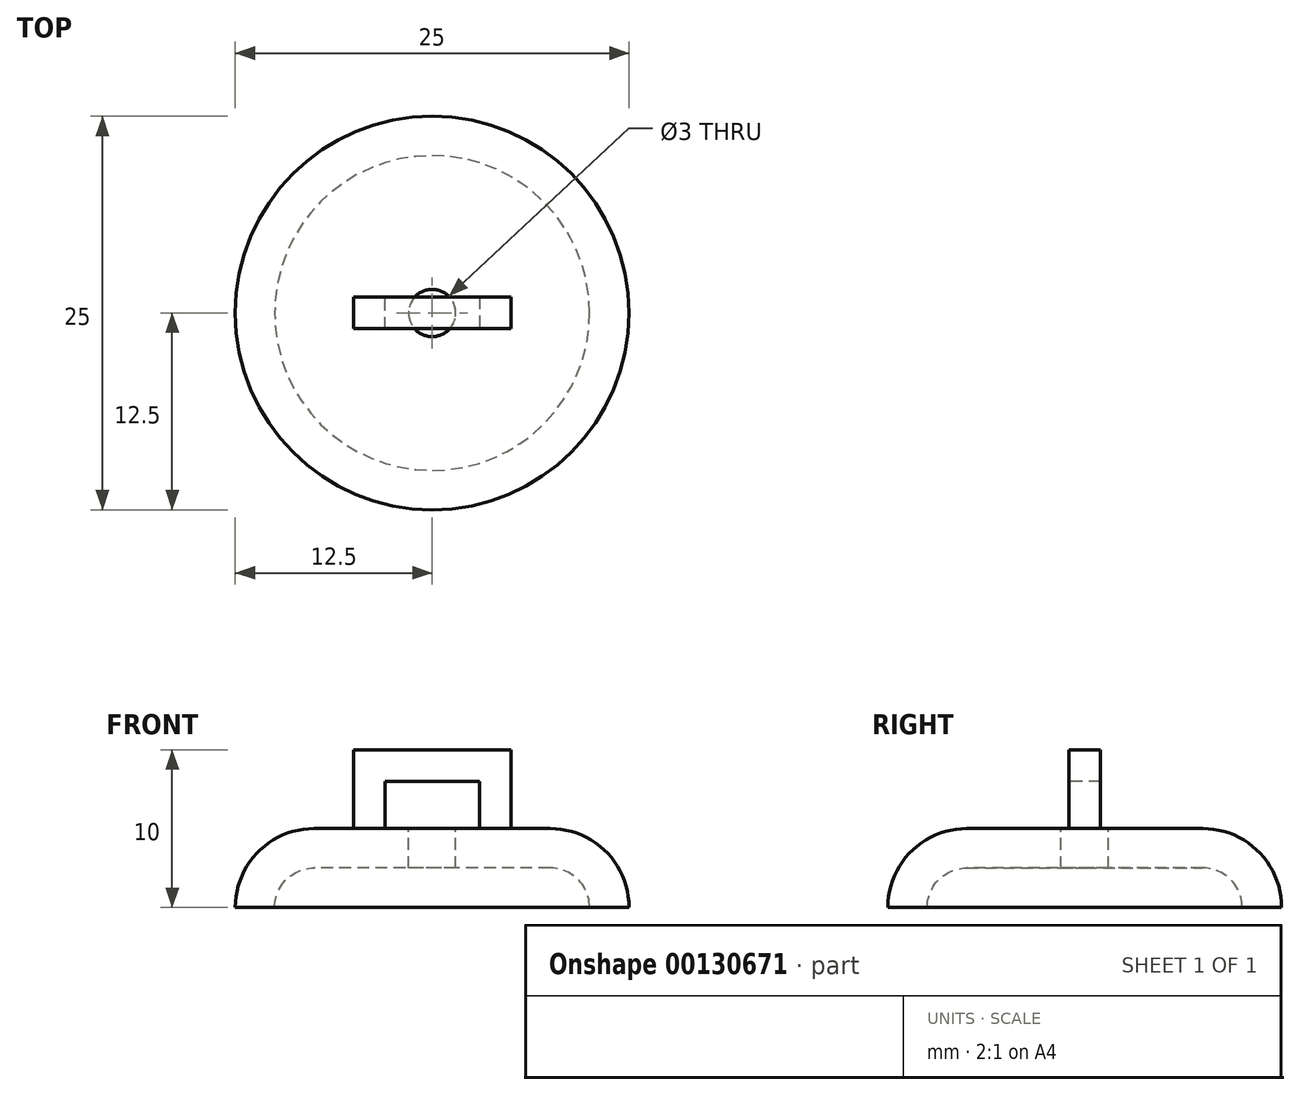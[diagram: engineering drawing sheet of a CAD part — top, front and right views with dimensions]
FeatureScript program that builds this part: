
annotation { "Feature Type Name" : "Feature", "Feature Type Description" : "" }
export const myFeature = defineFeature(function(context is Context, id is Id, definition is map)
    precondition{}
    {
        {
            var Q0;
            Q0=qCreatedBy(makeId("Top.planeOp"),FACE);
            var sketch = newSketch(context, id + "F0", { "sketchPlane" : qUnion([Q0])});
            skCircle(sketch, "E0", {"center": v(0, 0) * mm, "radius": 12.5 * mm});
            skSolve(sketch);
        }
        {
            var Q0;
            Q0 = qSketchRegion(id + "F0", true);
            extrude(context, id + "F1", {"entities" : qUnion([Q0]), "depth" : 5 * mm});
        }
        {
            var Q0;
            Q0=makeQuery(id+"F1.opExtrude","CAP_FACE",FACE,{"disambiguationData":[OSD([sQuery(id+"F0.wireOp",EDGE,"E0")])],"isStart":false});
            fillet(context, id + "F2", {"entities" : qUnion([Q0]), "radius" : 5 * mm, "tangentPropagation" : true, "allowEdgeOverflow" : false});
        }
        {
            var Q0;
            Q0=makeQuery(id+"F1.opExtrude","CAP_FACE",FACE,{"disambiguationData":[OSD([sQuery(id+"F0.wireOp",EDGE,"E0")])],"isStart":true});
            shell(context, id + "F3", {"entities" : qUnion([Q0]), "thickness" : 2.5 * mm});
        }
        {
            var Q0;
            Q0=makeQuery(id+"F1.opExtrude","CAP_FACE",FACE,{"disambiguationData":[OSD([sQuery(id+"F0.wireOp",EDGE,"E0")])],"isStart":false});
            var sketch = newSketch(context, id + "F4", { "sketchPlane" : qUnion([Q0])});
            skCircle(sketch, "E1", {"center": v(0, 0) * mm, "radius": 1.5 * mm});
            skSolve(sketch);
        }
        {
            var Q0;
            Q0 = qSketchRegion(id + "F4", true);
            extrude(context, id + "F5", {"entities" : qUnion([Q0]), "operationType" : NewBodyOperationType.REMOVE, "oppositeDirection" : true, "depth" : 25 * mm});
        }
        {
            var Q0;
            Q0=makeQuery(id+"F1.opExtrude","CAP_FACE",FACE,{"disambiguationData":[OSD([sQuery(id+"F0.wireOp",EDGE,"E0")])],"isStart":false});
            var sketch = newSketch(context, id + "F6", { "sketchPlane" : qUnion([Q0])});
            skLineSegment(sketch, "E2.bottom", {"start": v(5, 1) * mm, "end": v(3, 1) * mm});
            skLineSegment(sketch, "E2.top", {"start": v(5, -1) * mm, "end": v(3, -1) * mm});
            skLineSegment(sketch, "E2.left", {"start": v(5, 1) * mm, "end": v(5, -1) * mm});
            skLineSegment(sketch, "E2.right", {"start": v(3, 1) * mm, "end": v(3, -1) * mm});
            skPoint(sketch, "E2.middle", {"position": v(4, 0) * mm});
            skLineSegment(sketch, "E3.bottom", {"start": v(-5, -1) * mm, "end": v(-3, -1) * mm});
            skLineSegment(sketch, "E3.top", {"start": v(-5, 1) * mm, "end": v(-3, 1) * mm});
            skLineSegment(sketch, "E3.left", {"start": v(-5, -1) * mm, "end": v(-5, 1) * mm});
            skLineSegment(sketch, "E3.right", {"start": v(-3, -1) * mm, "end": v(-3, 1) * mm});
            skPoint(sketch, "E3.middle", {"position": v(-4, 0) * mm});
            skPoint(sketch, "E3.middle.positionSnap0", {"position": v(3, 0) * mm});
            skPoint(sketch, "E3.centerSnap0", {"position": v(3, 0) * mm});
            skSolve(sketch);
        }
        {
            var Q0;
            Q0 = qSketchRegion(id + "F6", true);
            extrude(context, id + "F7", {"entities" : qUnion([Q0]), "operationType" : NewBodyOperationType.ADD, "depth" : 5 * mm});
        }
        {
            var Q0;
            Q0=makeQuery(id+"F7.opExtrude","SWEPT_FACE",FACE,{"disambiguationData":[OSD([sQuery(id+"F6.wireOp",EDGE,"E2.left")])]});
            var sketch = newSketch(context, id + "F8", { "sketchPlane" : qUnion([Q0])});
            skLineSegment(sketch, "E4.bottom", {"start": v(1, 10) * mm, "end": v(-1, 10) * mm});
            skLineSegment(sketch, "E4.top", {"start": v(1, 8) * mm, "end": v(-1, 8) * mm});
            skLineSegment(sketch, "E4.left", {"start": v(1, 10) * mm, "end": v(1, 8) * mm});
            skLineSegment(sketch, "E4.right", {"start": v(-1, 10) * mm, "end": v(-1, 8) * mm});
            skSolve(sketch);
        }
        {
            var Q0;
            Q0 = qSketchRegion(id + "F8", true);
            extrude(context, id + "F9", {"entities" : qUnion([Q0]), "operationType" : NewBodyOperationType.ADD, "oppositeDirection" : true, "depth" : 10 * mm});
        }
    });
